FCSTD DOCUMENT  (FreeCAD 0.19R24291 (Git))
Label: data
License: All rights reserved
LicenseURL: http://en.wikipedia.org/wiki/All_rights_reserved
objects: Spreadsheet::Sheet×1

FEATURE [Spreadsheet::Sheet] Spreadsheet  label="data"
  cells = A2=WallThickness; B2(WallThickness)==2.4mm; C2=Planning on 0.4mm nozzle; A4=M3Diameter; B4(M3Diameter)==3mm; A5=M3DiameterTap; B5(M3DiameterTap)==2.8mm; A6=M3DiameterHole; B6(M3DiameterHole)==3.4mm; A7=M4Diameter; B7(M4Diameter)==4mm; A8=M4DiameterTap; B8(M4DiameterTap)==3.8mm; A9=M4DiameterHole; B9(M4DiameterHole)==4.2mm; A11=StepperShaftDiameter; B11(StepperShaftDiameter)==5.2mm; C11=Round diameter of stepper shaft; A12=StepperShaftRectWidth; B12(StepperShaftRectWidth)==3.2mm; C12=thickness at the end of theshaft; A13=StepperShaftRoundLength; B13(StepperShaftRoundLength)==2.5mm; A14=StepperShaftRectLength; B14(StepperShaftRectLength)==6mm; A15=StepperShaftOffset; B15(StepperShaftOffset)==8mm; C15=Distance from stepper mount centerline to stepper shaft center; A16=StepperMountWidth; B16(StepperMountWidth)==35mm; C16=Distance between mount hole centers; A17=StepperMountDiameter; B17(StepperMountDiameter)==4.4mm; A18=StepperMountOutsideDiameter; B18(StepperMountOutsideDiameter)==7mm; A19=StepperMountSpacerHole; B19(StepperMountSpacerHole)==M4Diameter; A20=StepperMountHeight; B20(StepperMountHeight)==20mm + 3mm; A21=StepperMountThickness; B21(StepperMountThickness)==0.5mm; A22=StepperMountToGear01Dist; B22(StepperMountToGear01Dist)==2.4mm; C22=vertical distance from stepper mount to gear01; A24=GearModule; B24(GearModule)=1; A26=Gear01Teeth; B26(Gear01Teeth)=15; A27=Gear01Thickness; B27(Gear01Thickness)==StepperShaftRoundLength + StepperShaftRectLength; A28=Gear01Diameter; B28(Gear01Diameter)==GearModule * (Gear01Teeth + 2) * 1mm; A30=Gear02Teeth; B30(Gear02Teeth)=30; A31=Gear02Diameter; B31(Gear02Diameter)==GearModule * (Gear02Teeth + 2) * 1mm; A32=Gear02Thickness; B32(Gear02Thickness)==7mm; A33=Gear02Tol; B33(Gear02Tol)==0.2mm; A34=Gear02MountDiameter; B34(Gear02MountDiameter)==10mm; A35=Gear02ShaftDiameter; B35(Gear02ShaftDiameter)==6mm; A36=Gear02ShaftHole; B36(Gear02ShaftHole)==Gear02ShaftDiameter + 0.2mm; A37=Gear02ShaftLength; B37(Gear02ShaftLength)==Gear02Thickness + Gear02Tol; A38=Gear02LeverOffset; B38(Gear02LeverOffset)==Gear02ShaftDiameter / 2 + 1mm; A39=Gear02LeverWidth; B39(Gear02LeverWidth)==10mm; A40=Gear02LeverLength; B40(Gear02LeverLength)==80mm; A41=Gear02NotchOffset; B41(Gear02NotchOffset)==1mm; A42=Gear02NotchCornerRadius; B42(Gear02NotchCornerRadius)==1.2mm; A43=Gear02SlotStart; B43(Gear02SlotStart)==Gear02LeverOffset + Gear02LeverLength - Gear02NotchOffset - Gear02NotchCornerRadius; A44=Gear02SlotDiameter; B44(Gear02SlotDiameter)==Gear02Thickness / 3; A45=Gear02SlotDepth; B45(Gear02SlotDepth)==1mm; A47=Gear01to02Dist; B47(Gear01to02Dist)==(GearModule * Gear01Teeth / 2 + GearModule * Gear02Teeth / 2) * 1mm; C47=Distance between gear centers; A48=Gear02Dist; B48(Gear02Dist)==StepperShaftOffset + Gear01to02Dist; C48=Distance from Stepper mount centerline to gear 02 center; A49=Gear02Height; B49(Gear02Height)==StepperMountHeight + StepperMountToGear01Dist; C49=Distance from back to gear02; A51=MagnetDiameter; B51(MagnetDiameter)==5mm; A52=MagnetThickness; B52(MagnetThickness)==3mm; A53=MagnetAngle; B53(MagnetAngle)==95deg; A54=MagnetDistanceOnGear; B54(MagnetDistanceOnGear)==GearModule * Gear02Teeth / 2 * 1mm - MagnetDiameter / 2 - 2mm; A56=PCBThickness; B56(PCBThickness)==1.6mm; A57=PCBWidth; B57(PCBWidth)==60mm; A58=PCBLength; B58(PCBLength)==100mm; A59=PCBGear02X; B59(PCBGear02X)==3.7mm; C59=Offset from right edge of board to Gear02 center; A60=PCBGear02Y; B60(PCBGear02Y)==21.7mm; C60=Offset from top of board to Gear02 center; A61=PCBMountY; B61(PCBMountY)==5mm; C61=Offset from bottom of board to center of mounts; A62=PCBMount1X; B62(PCBMount1X)==16mm; C62=Offset from left of board to mount1 center; A63=PCBMount2X; B63(PCBMount2X)==5mm; C63=Offset from right of board to mount2 center; A64=PCBMountInsideDiameter; B64(PCBMountInsideDiameter)==M3DiameterTap; A65=PCBMountOutsideDiameter; B65(PCBMountOutsideDiameter)==7mm; A66=PCBOffset; B66(PCBOffset)==1mm; C66=Distance from top and left PCB edge to inside wall; A67=PCBOffsetGearSide; B67(PCBOffsetGearSide)==7mm; C67=offset on the side of gear 2; A68=PCBHeight; B68(PCBHeight)==Gear02Height + Gear02Thickness + Gear02Tol + HallSensorGap; A69=PCBStepperSpacerLength; B69(PCBStepperSpacerLength)==PCBHeight - StepperMountHeight - StepperMountThickness; A70=PCBPowerJackY; B70(PCBPowerJackY)==5.75mm; C70=Offset from bottom of board to power jack; A72=PowerJackHeight; B72(PowerJackHeight)==11mm; A73=PowerJackWidth; B73(PowerJackWidth)==9.5mm; A74=HallSensorGap; B74(HallSensorGap)==2mm; A76=KnobDiameter; B76(KnobDiameter)==24mm; A77=KnobHeight; B77(KnobHeight)==10mm; A78=KnobCornerRadius; B78(KnobCornerRadius)==1mm; A79=KnobShaftOutsideDiameter; B79(KnobShaftOutsideDiameter)==10mm; A80=KnobShaftLength; B80(KnobShaftLength)==3.2mm + WallThickness; A81=KnobShaftDiameter; B81(KnobShaftDiameter)==6.4mm; A82=KnobShaftCut; B82(KnobShaftCut)==1.5mm; A83=KnobShaftDepth; B83(KnobShaftDepth)==12mm; A84=KnobShaftDiameter2; B84(KnobShaftDiameter2)==7mm; A85=KnobShaftDepth2; B85(KnobShaftDepth2)==4.5mm; A86=KnobShaftTol; B86(KnobShaftTol)==1mm; C86=Extra diameter for hole in front; A87=KnobHoleDiameter; B87(KnobHoleDiameter)==KnobShaftOutsideDiameter + KnobShaftTol; A88=KnobShaftOffsetX; B88(KnobShaftOffsetX)==WallThickness + PCBOffset + 31.6mm; A89=KnobShaftOffsetY; B89(KnobShaftOffsetY)==WallThickness + PCBOffset + 72.59999999999999mm; A91=LCDPCBThickness; B91(LCDPCBThickness)==1.6mm; A92=LCDGlassThickness; B92(LCDGlassThickness)==1.75mm; A93=LCDThickness; B93(LCDThickness)==LCDPCBThickness + LCDGlassThickness; C93=Distance from top of glass to bottom of PCB; A94=LCDMountLength; B94(LCDMountLength)==PCBHeight + PCBThickness + PowerJackHeight - LCDThickness; A95=LCDWidth; B95(LCDWidth)==35mm; A96=LCDLength; B96(LCDLength)==32mm; A97=LCDMountInsideDiameter; B97(LCDMountInsideDiameter)==M3DiameterTap; A98=LCDMountOutsideDiameter; B98(LCDMountOutsideDiameter)==6.4mm; A99=LCDMountOffset; B99(LCDMountOffset)==2.5mm; A100=LCDMountDistX; B100(LCDMountDistX)==30mm; A101=LCDMountDistY; B101(LCDMountDistY)==27mm; A102=LCDMountOffsetX; B102(LCDMountOffsetX)==(InsideWidth - LCDMountDistX) / 2; A103=LCDMountOffsetY; +35 more cells
